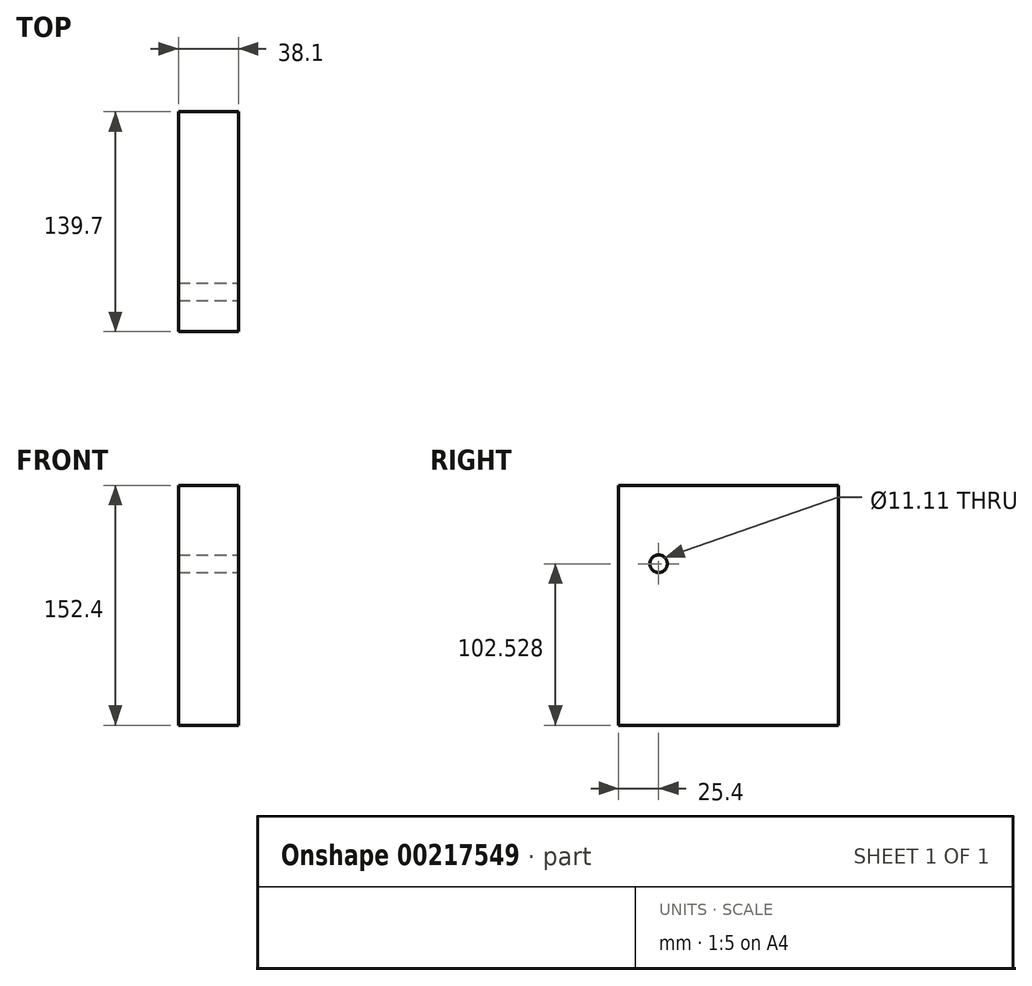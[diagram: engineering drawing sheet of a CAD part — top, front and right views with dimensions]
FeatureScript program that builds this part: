
annotation { "Feature Type Name" : "Feature", "Feature Type Description" : "" }
export const myFeature = defineFeature(function(context is Context, id is Id, definition is map)
    precondition{}
    {
        {
            var Q0;
            Q0=qCreatedBy(makeId("Top.planeOp"),FACE);
            var sketch = newSketch(context, id + "F0", { "sketchPlane" : qUnion([Q0])});
            skLineSegment(sketch, "E0.bottom", {"start": v(0, 0) * mm, "end": v(38.1, 0) * mm});
            skLineSegment(sketch, "E0.top", {"start": v(0, 139.7) * mm, "end": v(38.1, 139.7) * mm});
            skLineSegment(sketch, "E0.left", {"start": v(0, 0) * mm, "end": v(0, 139.7) * mm});
            skLineSegment(sketch, "E0.right", {"start": v(38.1, 0) * mm, "end": v(38.1, 139.7) * mm});
            skSolve(sketch);
        }
        {
            var Q0;
            Q0=makeQuery(id+"F0.imprint","IMPRINT",FACE,{"disambiguationData":[TD([[makeQuery(id+"F0.imprint","IMPRINT",EDGE,{"derivedFrom":sQuery(id+"F0.wireOp",EDGE,"E0.bottom")}),1.0]])]});
            extrude(context, id + "F1", {"entities" : qUnion([Q0]), "depth" : 152.4 * mm});
        }
        {
            var Q0;
            Q0=makeQuery(id+"F1.opExtrude","SWEPT_FACE",FACE,{"disambiguationData":[OSD([sQuery(id+"F0.wireOp",EDGE,"E0.right")])]});
            var sketch = newSketch(context, id + "F2", { "sketchPlane" : qUnion([Q0])});
            skCircle(sketch, "E1", {"center": v(25.4, 102.53) * mm, "radius": 5.55 * mm});
            skSolve(sketch);
        }
        {
            var Q0;
            Q0 = qSketchRegion(id + "F2", true);
            extrude(context, id + "F3", {"entities" : qUnion([Q0]), "operationType" : NewBodyOperationType.REMOVE, "oppositeDirection" : true, "depth" : 76.2 * mm});
        }
    });
